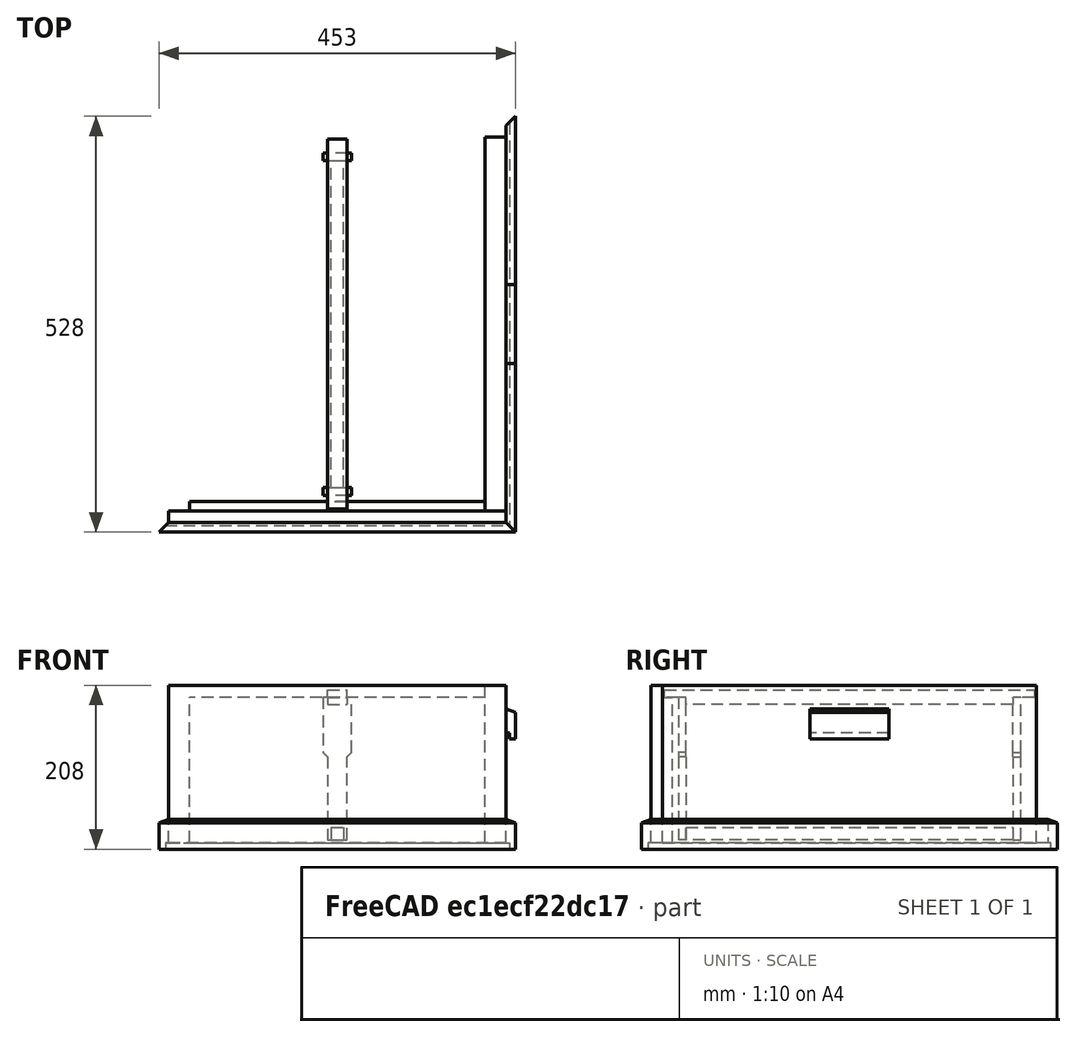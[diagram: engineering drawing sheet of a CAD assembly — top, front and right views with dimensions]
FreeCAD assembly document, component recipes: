
FREECAD ASSEMBLY — COMPONENT RECIPES ("naklada_nizka")

This assembly document has 6 components, labeled P0..P5 below (a component is one placed body or linked part). 6 of them carry a construction recipe — the FreeCAD feature program that regenerates the part from scratch, quoted from this document or its linked companion documents; the rest are supplied as boundary geometry only. No exploded tour is included for this assembly.
COMPONENT P0 — recipe-attached ("slat_side", modeled in this document).
Construction recipe (the document's own serialized feature program — sketch geometry with constraints, then the solid features built on it; lengths are millimeters unless a unit is written):

FEATURE [PartDesign::CoordinateSystem] LCS_0005
  AttacherType = Attacher::AttachEngine3D
  MapMode = 2
  Support = -> [X_Axis006]
FEATURE [Sketcher::SketchObject] Sketch003  label="Sketch004"
  FullyConstrained = true
  MapMode = 5
  Placement = pos=(0,0,0) rot=(1,0,0;1.5708rad)
  Support = -> [XZ_Plane006]
  expr: Constraints[12] = Variables.inner_width / 2 + Variables.wall_thickness
  sketch-geometry (6):
    g0: LineSegment StartX=214.5 StartY=0 StartZ=0 EndX=218.5 EndY=0 EndZ=0
    g1: LineSegment StartX=218.5 StartY=0 StartZ=0 EndX=218.5 EndY=-8 EndZ=0
    g2: LineSegment StartX=218.5 StartY=-8 StartZ=0 EndX=226.5 EndY=-8 EndZ=0
    g3: LineSegment StartX=226.5 StartY=-8 StartZ=0 EndX=226.5 EndY=25.6324 EndZ=0
    g4: LineSegment StartX=214.5 StartY=30 StartZ=0 EndX=214.5 EndY=0 EndZ=0
    g5: LineSegment StartX=214.5 StartY=30 StartZ=0 EndX=226.5 EndY=25.6324 EndZ=0
  constraints (18):
    c: Horizontal(g0)
    c: Coincident(g0,g1)
    c: Vertical(g1)
    c: Coincident(g1,g2)
    c: Horizontal(g2)
    c: Coincident(g2,g3)
    c: Vertical(g3)
    c: Coincident(g4,g0)
    c: Vertical(g4)
    c: DistanceX(g0,g0) = 4  'c'
    c: DistanceY(g1,g1) = 8  'd'
    c: Horizontal(g0,g-1)
    c: DistanceX(g-1,g0) = 214.5
    c: DistanceX(g0,g2) = 12  'a'
    c: DistanceY(g4,g4) = 30  'b'
    c: Coincident(g5,g4)
    c: Coincident(g5,g3)
    c: Angle(g5) = -0.349066  'e'
FEATURE [PartDesign::Pad] Pad002
  Direction = (1,1,1)
  Length = 700
  Length2 = 100
  Midplane = true
  Placement = pos=(0,0,0) rot=(1,0,0;1.5708rad)
  Profile = -> Sketch003
  Type = 0
FEATURE [Sketcher::SketchObject] Sketch004  label="Sketch005"
  ExternalGeometry = -> [Pad002]
  FullyConstrained = true
  MapMode = 5
  Support = -> [XY_Plane006]
  expr: Constraints[14] = Variables.inner_depth + 2 * Variables.wall_thickness
  sketch-geometry (8):
    g0: LineSegment StartX=226.5 StartY=-350 StartZ=0 EndX=226.5 EndY=-264 EndZ=0
    g1: LineSegment StartX=226.5 StartY=-264 StartZ=0 EndX=214.5 EndY=-252 EndZ=0
    g2: LineSegment StartX=214.5 StartY=-252 StartZ=0 EndX=214.5 EndY=-350 EndZ=0
    g3: LineSegment StartX=226.5 StartY=350 StartZ=0 EndX=226.5 EndY=264 EndZ=0
    g4: LineSegment StartX=226.5 StartY=264 StartZ=0 EndX=214.5 EndY=252 EndZ=0
    g5: LineSegment StartX=214.5 StartY=252 StartZ=0 EndX=214.5 EndY=350 EndZ=0
    g6: LineSegment StartX=214.5 StartY=-350 StartZ=0 EndX=226.5 EndY=-350 EndZ=0
    g7: LineSegment StartX=214.5 StartY=350 StartZ=0 EndX=226.5 EndY=350 EndZ=0
  constraints (20):
    c: Coincident(g0,g-4)
    c: Coincident(g1,g0)
    c: Coincident(g2,g1)
    c: Coincident(g2,g-4)
    c: Vertical(g2)
    c: Vertical(g0)
    c: Coincident(g-3,g3)
    c: Vertical(g3)
    c: Coincident(g3,g4)
    c: Coincident(g4,g5)
    c: Coincident(g5,g-3)
    c: Vertical(g5)
    c: Equal(g4,g1)
    c: Equal(g5,g2)
    c: DistanceY(g1,g4) = 504
    c: Coincident(g6,g2)
    c: Coincident(g6,g0)
    c: Coincident(g7,g5)
    c: Coincident(g7,g3)
    c: Perpendicular(g4,g1)
FEATURE [PartDesign::Pocket] Pocket001
  BaseFeature = -> Pad002
  Length = 41
  Length2 = 100
  Midplane = true
  Placement = pos=(0,0,0) rot=(1,0,0;1.5708rad)
  Profile = -> Sketch004
  Type = 1
FEATURE [PartDesign::Body] Body_3
  Group = -> [LCS_0005,Sketch003,Pad002,Sketch004,Pocket001]
  Origin = -> Origin006
  Tip = -> Pocket001
COMPONENT P1 — recipe-attached ("slat_front_rear", modeled in this document).
Construction recipe (the document's own serialized feature program — sketch geometry with constraints, then the solid features built on it; lengths are millimeters unless a unit is written):

FEATURE [PartDesign::CoordinateSystem] LCS_0007
  AttacherType = Attacher::AttachEngine3D
  MapMode = 2
  Support = -> [X_Axis008]
FEATURE [Sketcher::SketchObject] Sketch005  label="Sketch006"
  FullyConstrained = true
  MapMode = 5
  Placement = pos=(0,0,0) rot=(0.57735,0.57735,0.57735;2.0944rad)
  Support = -> [YZ_Plane008]
  expr: Constraints[17] = Variables.inner_depth / 2 + Variables.wall_thickness
  sketch-geometry (6):
    g0: LineSegment StartX=-252 StartY=0 StartZ=0 EndX=-252 EndY=30 EndZ=0
    g1: LineSegment StartX=-264 StartY=25.6324 StartZ=0 EndX=-264 EndY=-8 EndZ=0
    g2: LineSegment StartX=-264 StartY=-8 StartZ=0 EndX=-256 EndY=-8 EndZ=0
    g3: LineSegment StartX=-256 StartY=-8 StartZ=0 EndX=-256 EndY=0 EndZ=0
    g4: LineSegment StartX=-256 StartY=0 StartZ=0 EndX=-252 EndY=0 EndZ=0
    g5: LineSegment StartX=-264 StartY=25.6324 StartZ=0 EndX=-252 EndY=30 EndZ=0
  constraints (18):
    c: Vertical(g0)
    c: Vertical(g1)
    c: Coincident(g1,g2)
    c: Horizontal(g2)
    c: Coincident(g2,g3)
    c: Vertical(g3)
    c: Coincident(g3,g4)
    c: Coincident(g4,g0)
    c: Horizontal(g4)
    c: Horizontal(g0,g-1)
    c: DistanceX(g4,g4) = 4
    c: DistanceY(g3,g3) = 8
    c: DistanceX(g1,g0) = 12
    c: DistanceY(g0,g0) = 30
    c: Coincident(g5,g1)
    c: Coincident(g5,g0)
    c: Angle(g5) = 0.349066
    c: DistanceX(g0,g-1) = 252
FEATURE [PartDesign::Pad] Pad003
  Direction = (1,1,1)
  Length = 700
  Length2 = 100
  Midplane = true
  Placement = pos=(0,0,0) rot=(0.57735,0.57735,0.57735;2.0944rad)
  Profile = -> Sketch005
  Type = 0
FEATURE [Sketcher::SketchObject] Sketch006  label="Sketch007"
  ExternalGeometry = -> [Pad003]
  FullyConstrained = true
  MapMode = 5
  Support = -> [XY_Plane008]
  expr: Constraints[19] = Variables.inner_width + 2 * Variables.wall_thickness
  sketch-geometry (8):
    g0: LineSegment StartX=-350 StartY=-264 StartZ=0 EndX=-350 EndY=-252 EndZ=0
    g1: LineSegment StartX=-350 StartY=-252 StartZ=0 EndX=-214.5 EndY=-252 EndZ=0
    g2: LineSegment StartX=-214.5 StartY=-252 StartZ=0 EndX=-226.5 EndY=-264 EndZ=0
    g3: LineSegment StartX=-226.5 StartY=-264 StartZ=0 EndX=-350 EndY=-264 EndZ=0
    g4: LineSegment StartX=350 StartY=-264 StartZ=0 EndX=350 EndY=-252 EndZ=0
    g5: LineSegment StartX=350 StartY=-252 StartZ=0 EndX=214.5 EndY=-252 EndZ=0
    g6: LineSegment StartX=214.5 StartY=-252 StartZ=0 EndX=226.5 EndY=-264 EndZ=0
    g7: LineSegment StartX=226.5 StartY=-264 StartZ=0 EndX=350 EndY=-264 EndZ=0
  constraints (20):
    c: Coincident(g-3,g0)
    c: Coincident(g0,g-3)
    c: Coincident(g0,g1)
    c: Coincident(g1,g2)
    c: Coincident(g2,g3)
    c: Coincident(g3,g0)
    c: Coincident(g-4,g4)
    c: Coincident(g4,g-4)
    c: Coincident(g4,g5)
    c: Coincident(g5,g6)
    c: Coincident(g6,g7)
    c: Coincident(g7,g4)
    c: Perpendicular(g2,g6)
    c: Equal(g2,g6)
    c: Equal(g1,g5)
    c: Horizontal(g1)
    c: Horizontal(g3)
    c: Horizontal(g7)
    c: Horizontal(g5)
    c: DistanceX(g1,g5) = 429
FEATURE [PartDesign::Pocket] Pocket002
  BaseFeature = -> Pad003
  Length = 5
  Length2 = 100
  Midplane = true
  Placement = pos=(0,0,0) rot=(0.57735,0.57735,0.57735;2.0944rad)
  Profile = -> Sketch006
  Type = 1
FEATURE [PartDesign::Body] Body_4
  Group = -> [LCS_0007,Sketch005,Pad003,Sketch006,Pocket002]
  Origin = -> Origin008
  Tip = -> Pocket002
COMPONENT P2 — recipe-attached ("handle", modeled in this document).
Construction recipe (the document's own serialized feature program — sketch geometry with constraints, then the solid features built on it; lengths are millimeters unless a unit is written):

FEATURE [Sketcher::SketchObject] Sketch007  label="Sketch008"
  FullyConstrained = true
  MapMode = 5
  Placement = pos=(0,0,0) rot=(1,0,0;1.5708rad)
  Support = -> [XZ_Plane009]
  expr: Constraints[11] = Variables.inner_width / 2 + Variables.wall_thickness
  expr: Constraints[17] = Variables.height - 30
  sketch-geometry (6):
    g0: LineSegment StartX=214.5 StartY=140 StartZ=0 EndX=218.5 EndY=140 EndZ=0
    g1: LineSegment StartX=218.5 StartY=140 StartZ=0 EndX=218.5 EndY=132 EndZ=0
    g2: LineSegment StartX=218.5 StartY=132 StartZ=0 EndX=226.5 EndY=132 EndZ=0
    g3: LineSegment StartX=226.5 StartY=132 StartZ=0 EndX=226.5 EndY=165.632 EndZ=0
    g4: LineSegment StartX=214.5 StartY=170 StartZ=0 EndX=214.5 EndY=140 EndZ=0
    g5: LineSegment StartX=214.5 StartY=170 StartZ=0 EndX=226.5 EndY=165.632 EndZ=0
  constraints (18):
    c: Horizontal(g0)
    c: Coincident(g0,g1)
    c: Vertical(g1)
    c: Coincident(g1,g2)
    c: Horizontal(g2)
    c: Coincident(g2,g3)
    c: Vertical(g3)
    c: Coincident(g4,g0)
    c: Vertical(g4)
    c: DistanceX(g0,g0) = 4  'c'
    c: DistanceY(g1,g1) = 8  'd'
    c: DistanceX(g-1,g0) = 214.5
    c: DistanceX(g0,g2) = 12  'a'
    c: DistanceY(g4,g4) = 30  'b'
    c: Coincident(g5,g4)
    c: Coincident(g5,g3)
    c: Angle(g5) = -0.349066  'e'
    c: DistanceY(g-1,g4) = 170
FEATURE [PartDesign::CoordinateSystem] LCS_0008
  AttacherType = Attacher::AttachEngine3D
  MapMode = 2
  Support = -> [X_Axis010]
FEATURE [PartDesign::Pad] Pad004
  Direction = (1,1,1)
  Length = 100
  Length2 = 100
  Midplane = true
  Placement = pos=(0,0,0) rot=(1,0,0;1.5708rad)
  Profile = -> Sketch007
  Type = 0
FEATURE [PartDesign::Body] Body_005
  Group = -> [LCS_0008,Sketch007,Pad004]
  Origin = -> Origin009
  Tip = -> Pad004
COMPONENT P3 — recipe-attached ("wall_front_rear", modeled in this document).
Construction recipe (the document's own serialized feature program — sketch geometry with constraints, then the solid features built on it; lengths are millimeters unless a unit is written):

FEATURE [PartDesign::CoordinateSystem] LCS_0001
  AttacherType = Attacher::AttachEngine3D
  MapMode = 2
  Support = -> [X_Axis002]
FEATURE [Sketcher::SketchObject] Sketch  label="Sketch001"
  FullyConstrained = true
  MapMode = 5
  Support = -> [XY_Plane002]
  expr: Constraints[16] = Variables.inner_width
  expr: Constraints[17] = Variables.wall_thickness
  expr: Constraints[22] = Variables.inner_depth / 2
  expr: Constraints[19] = Variables.wall_thickness
  expr: Constraints[18] = Variables.wall_cut
  sketch-geometry (8):
    g0: LineSegment StartX=-187.5 StartY=-225 StartZ=0 EndX=187.5 EndY=-225 EndZ=0
    g1: LineSegment StartX=187.5 StartY=-225 StartZ=0 EndX=187.5 EndY=-237.5 EndZ=0
    g2: LineSegment StartX=187.5 StartY=-237.5 StartZ=0 EndX=214.5 EndY=-237.5 EndZ=0
    g3: LineSegment StartX=214.5 StartY=-237.5 StartZ=0 EndX=214.5 EndY=-252 EndZ=0
    g4: LineSegment StartX=214.5 StartY=-252 StartZ=0 EndX=-214.5 EndY=-252 EndZ=0
    g5: LineSegment StartX=-214.5 StartY=-252 StartZ=0 EndX=-214.5 EndY=-237.5 EndZ=0
    g6: LineSegment StartX=-214.5 StartY=-237.5 StartZ=0 EndX=-187.5 EndY=-237.5 EndZ=0
    g7: LineSegment StartX=-187.5 StartY=-237.5 StartZ=0 EndX=-187.5 EndY=-225 EndZ=0
  constraints (23):
    c: Coincident(g0,g1)
    c: Coincident(g1,g2)
    c: Horizontal(g2)
    c: Coincident(g2,g3)
    c: Vertical(g3)
    c: Coincident(g3,g4)
    c: Horizontal(g4)
    c: Coincident(g4,g5)
    c: Vertical(g5)
    c: Coincident(g5,g6)
    c: Horizontal(g6)
    c: Coincident(g6,g7)
    c: Vertical(g7)
    c: Vertical(g1)
    c: Horizontal(g6,g1)
    c: Equal(g6,g2)
    c: DistanceX(g0,g0) = 375
    c: DistanceX(g2,g2) = 27
    c: DistanceY(g1,g1) = 12.5
    c: DistanceY(g3,g0) = 27
    c: Coincident(g0,g7)
    c: Symmetric(g0,g0,g-2)
    c: DistanceY(g0,g-1) = 225
FEATURE [PartDesign::Pad] Pad
  Direction = (1,1,1)
  Length = 200
  Length2 = 100
  Profile = -> Sketch
  Type = 0
  expr: Length = Variables.height
FEATURE [Sketcher::SketchObject] Sketch001  label="Sketch002"
  ExternalGeometry = -> [Pad]
  FullyConstrained = true
  MapMode = 5
  Placement = pos=(0,0,0) rot=(0.57735,0.57735,0.57735;2.0944rad)
  Support = -> [YZ_Plane002]
  expr: Constraints[9] = Variables.frame_cut
  sketch-geometry (4):
    g0: LineSegment StartX=-225 StartY=200 StartZ=0 EndX=-237.5 EndY=200 EndZ=0
    g1: LineSegment StartX=-237.5 StartY=200 StartZ=0 EndX=-237.5 EndY=185 EndZ=0
    g2: LineSegment StartX=-237.5 StartY=185 StartZ=0 EndX=-225 EndY=185 EndZ=0
    g3: LineSegment StartX=-225 StartY=185 StartZ=0 EndX=-225 EndY=200 EndZ=0
  constraints (10):
    c: Coincident(g0,g1)
    c: Coincident(g1,g2)
    c: Coincident(g2,g3)
    c: Coincident(g3,g0)
    c: Horizontal(g2)
    c: Vertical(g1)
    c: Vertical(g3)
    c: Coincident(g0,g-3)
    c: Coincident(g0,g-3)
    c: DistanceY(g3,g3) = 15
FEATURE [PartDesign::Pocket] Pocket
  BaseFeature = -> Pad
  Length = 5
  Length2 = 100
  Midplane = true
  Profile = -> Sketch001
  Type = 1
FEATURE [PartDesign::Body] Body
  Group = -> [LCS_0001,Sketch,Pad,Sketch001,Pocket]
  Origin = -> Origin002
  Tip = -> Pocket
COMPONENT P4 — recipe-attached ("frame", modeled in this document).
Construction recipe (the document's own serialized feature program — sketch geometry with constraints, then the solid features built on it; lengths are millimeters unless a unit is written):

FEATURE [PartDesign::CoordinateSystem] LCS_0011
  AttacherType = Attacher::AttachEngine3D
  MapMode = 2
  Support = -> [X_Axis012]
FEATURE [Sketcher::SketchObject] Sketch008  label="Sketch009"
  FullyConstrained = true
  MapMode = 5
  Placement = pos=(0,0,0) rot=(0.57735,0.57735,0.57735;2.0944rad)
  Support = -> [YZ_Plane012]
  expr: Constraints[22] = Variables.height - Variables.frame_cut
  sketch-geometry (8):
    g0: LineSegment StartX=-235 StartY=194 StartZ=0 EndX=235 EndY=194 EndZ=0
    g1: LineSegment StartX=235 StartY=194 StartZ=0 EndX=235 EndY=185 EndZ=0
    g2: LineSegment StartX=235 StartY=185 StartZ=0 EndX=207.5 EndY=185 EndZ=0
    g3: LineSegment StartX=207.5 StartY=185 StartZ=0 EndX=207.5 EndY=176 EndZ=0
    g4: LineSegment StartX=207.5 StartY=176 StartZ=0 EndX=-207.5 EndY=176 EndZ=0
    g5: LineSegment StartX=-207.5 StartY=176 StartZ=0 EndX=-207.5 EndY=185 EndZ=0
    g6: LineSegment StartX=-207.5 StartY=185 StartZ=0 EndX=-235 EndY=185 EndZ=0
    g7: LineSegment StartX=-235 StartY=185 StartZ=0 EndX=-235 EndY=194 EndZ=0
  constraints (23):
    c: Horizontal(g0)
    c: Coincident(g0,g1)
    c: Vertical(g1)
    c: Coincident(g1,g2)
    c: Horizontal(g2)
    c: Coincident(g2,g3)
    c: Vertical(g3)
    c: Coincident(g3,g4)
    c: Horizontal(g4)
    c: Coincident(g4,g5)
    c: Vertical(g5)
    c: Coincident(g5,g6)
    c: Coincident(g6,g7)
    c: Coincident(g7,g0)
    c: Horizontal(g6)
    c: Vertical(g7)
    c: Symmetric(g5,g2,g-2)
    c: Equal(g6,g2)
    c: DistanceX(g0,g0) = 470
    c: DistanceX(g5,g2) = 415
    c: DistanceY(g1,g1) = 9
    c: DistanceY(g3,g0) = 18
    c: DistanceY(g-1,g6) = 185
FEATURE [PartDesign::Pad] Pad005
  Direction = (1,1,1)
  Length = 25
  Length2 = 100
  Midplane = true
  Placement = pos=(0,0,0) rot=(0.57735,0.57735,0.57735;2.0944rad)
  Profile = -> Sketch008
  Type = 0
FEATURE [Sketcher::SketchObject] Sketch010  label="Sketch011"
  ExternalGeometry = -> [Pad005]
  FullyConstrained = true
  MapMode = 5
  Placement = pos=(-9.13e-14,-207.5,4.57e-14) rot=(-0.57735,-0.57735,0.57735;4.18879rad)
  Support = -> [Pad005]
  expr: Constraints[21] = Variables.frame_height
  sketch-geometry (8):
    g0: LineSegment StartX=-185 StartY=18 StartZ=0 EndX=-185 EndY=-18 EndZ=0
    g1: LineSegment StartX=-185 StartY=-18 StartZ=0 EndX=-115 EndY=-18 EndZ=0
    g2: LineSegment StartX=-115 StartY=-18 StartZ=0 EndX=-109.5 EndY=-12.5 EndZ=0
    g3: LineSegment StartX=-109.5 StartY=-12.5 StartZ=0 EndX=-4 EndY=-12.5 EndZ=0
    g4: LineSegment StartX=-4 StartY=-12.5 StartZ=0 EndX=-4 EndY=12.5 EndZ=0
    g5: LineSegment StartX=-4 StartY=12.5 StartZ=0 EndX=-109.5 EndY=12.5 EndZ=0
    g6: LineSegment StartX=-109.5 StartY=12.5 StartZ=0 EndX=-115 EndY=18 EndZ=0
    g7: LineSegment StartX=-115 StartY=18 StartZ=0 EndX=-185 EndY=18 EndZ=0
  constraints (22):
    c: Coincident(g0,g1)
    c: Horizontal(g1)
    c: Coincident(g1,g2)
    c: Coincident(g2,g3)
    c: Horizontal(g3)
    c: Coincident(g3,g4)
    c: Coincident(g4,g5)
    c: Horizontal(g5)
    c: Coincident(g5,g6)
    c: Coincident(g6,g7)
    c: Coincident(g7,g0)
    c: Horizontal(g7)
    c: Vertical(g5,g2)
    c: Vertical(g1,g6)
    c: Symmetric(g0,g0,g-1)
    c: Symmetric(g4,g3,g-1)
    c: Perpendicular(g6,g2)
    c: DistanceY(g4,g4) = 25
    c: DistanceY(g0,g0) = 36
    c: DistanceX(g7,g7) = 70
    c: PointOnObject(g-3,g0)
    c: DistanceX(g-3,g4) = 190
FEATURE [PartDesign::Pad] Pad006
  BaseFeature = -> Pad005
  Direction = (1,1,1)
  Length = 10
  Length2 = 100
  Placement = pos=(0,0,0) rot=(0.57735,0.57735,0.57735;2.0944rad)
  Profile = -> Sketch010
  Type = 0
FEATURE [Sketcher::SketchObject] Sketch011  label="Sketch012"
  ExternalGeometry = -> [Pad006]
  FullyConstrained = true
  MapMode = 5
  Placement = pos=(1.143e-13,207.5,-4.56e-14) rot=(0.57735,0.57735,0.57735;4.18879rad)
  Support = -> [Pad006]
  sketch-geometry (8):
    g0: LineSegment StartX=4 StartY=12.5 StartZ=0 EndX=109.5 EndY=12.5 EndZ=0
    g1: LineSegment StartX=109.5 StartY=12.5 StartZ=0 EndX=115 EndY=18 EndZ=0
    g2: LineSegment StartX=115 StartY=18 StartZ=0 EndX=185 EndY=18 EndZ=0
    g3: LineSegment StartX=185 StartY=18 StartZ=0 EndX=185 EndY=-18 EndZ=0
    g4: LineSegment StartX=185 StartY=-18 StartZ=0 EndX=115 EndY=-18 EndZ=0
    g5: LineSegment StartX=115 StartY=-18 StartZ=0 EndX=109.5 EndY=-12.5 EndZ=0
    g6: LineSegment StartX=109.5 StartY=-12.5 StartZ=0 EndX=4 EndY=-12.5 EndZ=0
    g7: LineSegment StartX=4 StartY=-12.5 StartZ=0 EndX=4 EndY=12.5 EndZ=0
  constraints (17):
    c: Coincident(g-6,g0)
    c: Coincident(g0,g-3)
    c: Coincident(g0,g1)
    c: Coincident(g1,g-3)
    c: Coincident(g1,g2)
    c: Horizontal(g2)
    c: Coincident(g2,g3)
    c: Coincident(g3,g-5)
    c: Vertical(g3)
    c: Coincident(g3,g4)
    c: Coincident(g4,g-4)
    c: Coincident(g4,g5)
    c: Coincident(g5,g-4)
    c: Coincident(g5,g6)
    c: Coincident(g6,g-6)
    c: Coincident(g6,g7)
    c: Coincident(g7,g0)
FEATURE [PartDesign::Pad] Pad007
  BaseFeature = -> Pad006
  Direction = (1,1,1)
  Length = 10
  Length2 = 100
  Placement = pos=(0,0,0) rot=(0.57735,0.57735,0.57735;2.0944rad)
  Profile = -> Sketch011
  Type = 0
FEATURE [Sketcher::SketchObject] Sketch012  label="Sketch013"
  ExternalGeometry = -> [Pad007]
  FullyConstrained = true
  MapMode = 5
  Placement = pos=(0,0,0) rot=(0.57735,0.57735,0.57735;2.0944rad)
  Support = -> [YZ_Plane012]
  sketch-geometry (4):
    g0: LineSegment StartX=-207.5 StartY=20 StartZ=0 EndX=207.5 EndY=20 EndZ=0
    g1: LineSegment StartX=207.5 StartY=20 StartZ=0 EndX=207.5 EndY=4 EndZ=0
    g2: LineSegment StartX=207.5 StartY=4 StartZ=0 EndX=-207.5 EndY=4 EndZ=0
    g3: LineSegment StartX=-207.5 StartY=4 StartZ=0 EndX=-207.5 EndY=20 EndZ=0
  constraints (10):
    c: Coincident(g0,g1)
    c: Coincident(g1,g2)
    c: Coincident(g2,g3)
    c: Coincident(g3,g0)
    c: Horizontal(g0)
    c: Vertical(g1)
    c: Vertical(g3)
    c: Coincident(g1,g-4)
    c: Coincident(g2,g-3)
    c: DistanceY(g1,g1) = 16
FEATURE [PartDesign::Pad] Pad008
  BaseFeature = -> Pad007
  Direction = (1,1,1)
  Length = 16
  Length2 = 100
  Midplane = true
  Placement = pos=(0,0,0) rot=(0.57735,0.57735,0.57735;2.0944rad)
  Profile = -> Sketch012
  Type = 0
FEATURE [PartDesign::Body] Body_5
  Group = -> [LCS_0011,Sketch008,Pad005,Sketch010,Pad006,Sketch011,Pad007,Sketch012,Pad008]
  Origin = -> Origin012
  Tip = -> Pad008
COMPONENT P5 — recipe-attached ("wall_side", modeled in this document).
Construction recipe (the document's own serialized feature program — sketch geometry with constraints, then the solid features built on it; lengths are millimeters unless a unit is written):

FEATURE [PartDesign::CoordinateSystem] LCS_0003
  AttacherType = Attacher::AttachEngine3D
  MapMode = 2
  Support = -> [X_Axis004]
FEATURE [Sketcher::SketchObject] Sketch002  label="Sketch003"
  FullyConstrained = true
  MapMode = 5
  Support = -> [XY_Plane004]
  expr: Constraints[6] = Variables.wall_thickness
  expr: Constraints[7] = Variables.inner_depth + Variables.wall_cut * 2
  expr: Constraints[8] = Variables.inner_width / 2
  sketch-geometry (4):
    g0: LineSegment StartX=187.5 StartY=-237.5 StartZ=0 EndX=214.5 EndY=-237.5 EndZ=0
    g1: LineSegment StartX=214.5 StartY=-237.5 StartZ=0 EndX=214.5 EndY=237.5 EndZ=0
    g2: LineSegment StartX=214.5 StartY=237.5 StartZ=0 EndX=187.5 EndY=237.5 EndZ=0
    g3: LineSegment StartX=187.5 StartY=237.5 StartZ=0 EndX=187.5 EndY=-237.5 EndZ=0
  constraints (11):
    c: Coincident(g0,g1)
    c: Coincident(g1,g2)
    c: Coincident(g2,g3)
    c: Coincident(g3,g0)
    c: Horizontal(g0)
    c: Horizontal(g2)
    c: DistanceX(g0,g0) = 27
    c: DistanceY(g1,g1) = 475
    c: DistanceX(g-1,g0) = 187.5
    c: Vertical(g1)
    c: Symmetric(g0,g2,g-1)
FEATURE [PartDesign::Pad] Pad001
  Direction = (1,1,1)
  Length = 200
  Length2 = 100
  Profile = -> Sketch002
  Type = 0
  expr: Length = Variables.height
FEATURE [PartDesign::Body] Body_2
  Group = -> [LCS_0003,Sketch002,Pad001]
  Origin = -> Origin004
  Tip = -> Pad001
PROVENANCE & LICENSES
A FreeCAD (.FCStd) document from a public repository crawl; recipes are the document's own serialized feature recipes (and, for linked parts, companion documents' recipes).
License: apache-2.0.
